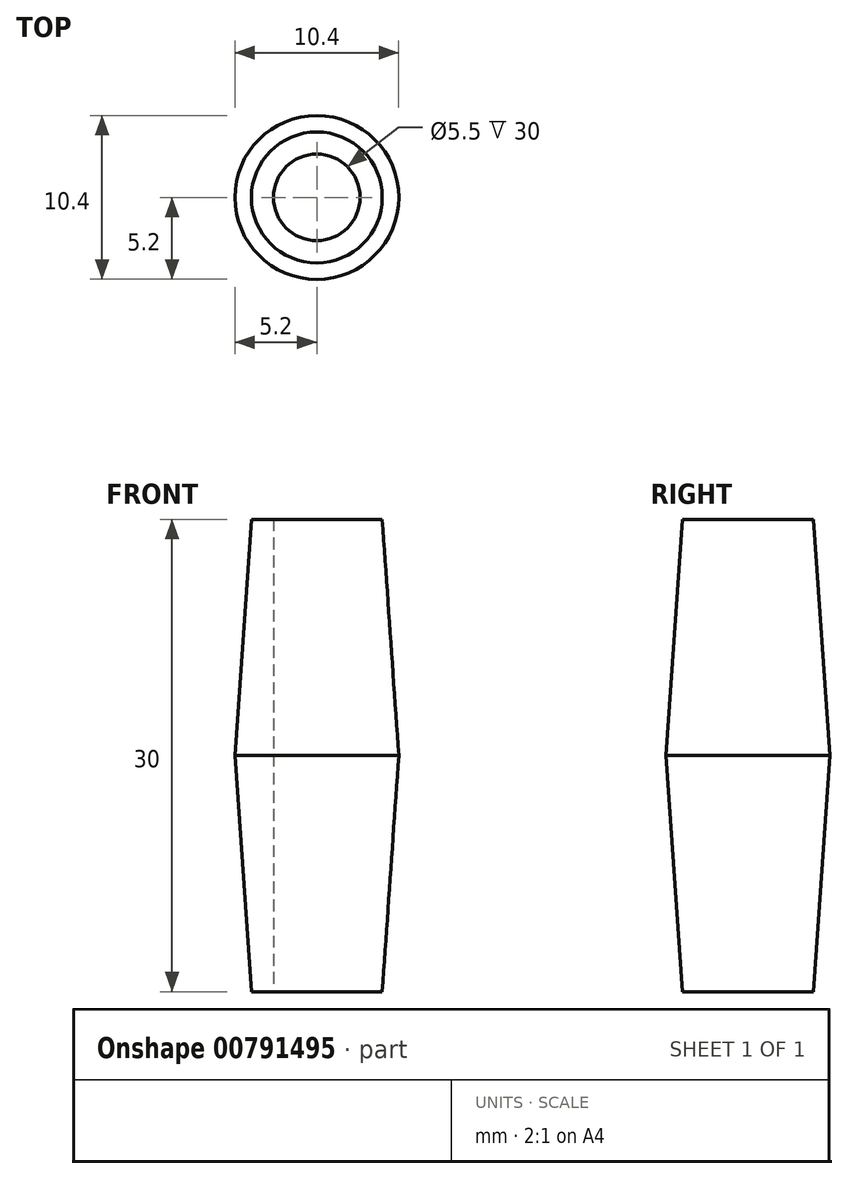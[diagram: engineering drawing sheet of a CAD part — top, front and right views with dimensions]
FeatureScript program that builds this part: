
annotation { "Feature Type Name" : "Feature", "Feature Type Description" : "" }
export const myFeature = defineFeature(function(context is Context, id is Id, definition is map)
    precondition{}
    {
        {
            var Q0;
            Q0=qCreatedBy(makeId("Top.planeOp"),FACE);
            var sketch = newSketch(context, id + "F0", { "sketchPlane" : qUnion([Q0])});
            skCircle(sketch, "E0", {"center": v(0, 0) * mm, "radius": 4.15 * mm});
            skSolve(sketch);
        }
        {
            var Q0;
            Q0=makeQuery(id+"F0.imprint","IMPRINT",FACE,{"disambiguationData":[TD([[makeQuery(id+"F0.imprint","IMPRINT",EDGE,{"derivedFrom":sQuery(id+"F0.wireOp",EDGE,"E0")}),1.0]])]});
            extrude(context, id + "F1", {"entities" : qUnion([Q0]), "depth" : 15 * mm, "offsetDistance" : 25 * mm, "hasDraft" : true, "draftAngle" : 4 * degree});
        }
        {
            var Q0;
            Q0=makeQuery(id+"F1.opExtrude","SWEPT_BODY",BODY,{"disambiguationData":[OSD([sQuery(id+"F0.wireOp",EDGE,"E0")])]});
            var Q1;
            Q1=makeQuery(id+"F1.opExtrude","CAP_FACE",FACE,{"disambiguationData":[OSD([sQuery(id+"F0.wireOp",EDGE,"E0")])],"isStart":false});
            mirror(context, id + "F2", {"operationType" : NewBodyOperationType.ADD, "entities" : qUnion([Q0]), "mirrorPlane" : qUnion([Q1])});
        }
        {
            var Q0;
            Q0=makeQuery(id+"F2.opPattern","COPY",FACE,{"derivedFrom":makeQuery(id+"F1.opExtrude","CAP_FACE",FACE,{"disambiguationData":[OSD([sQuery(id+"F0.wireOp",EDGE,"E0")])],"isStart":true}),"instanceName":"1"});
            var sketch = newSketch(context, id + "F3", { "sketchPlane" : qUnion([Q0])});
            skPoint(sketch, "E1", {"position": v(0, 0) * mm});
            skSolve(sketch);
        }
        {
            var Q0;
            Q0=sQuery(id+"F3.wireOp",VERTEX,"E1");
            var Q1;
            Q1=makeQuery(id+"F1.opExtrude","SWEPT_BODY",BODY,{"disambiguationData":[OSD([sQuery(id+"F0.wireOp",EDGE,"E0")])]});
            hole(context, id + "F4", {"style" : HoleStyle.SIMPLE, "endStyle" : HoleEndStyle.THROUGH, "holeDiameter" : 5.5 * mm, "majorDiameter" : 5 * mm, "isTappedThrough" : true, "tappedDepth" : 12 * mm, "tapClearance" : 3, "locations" : qUnion([Q0]), "scope" : qUnion([Q1]), "startStyle" : HoleStartStyle.PART});
        }
    });
